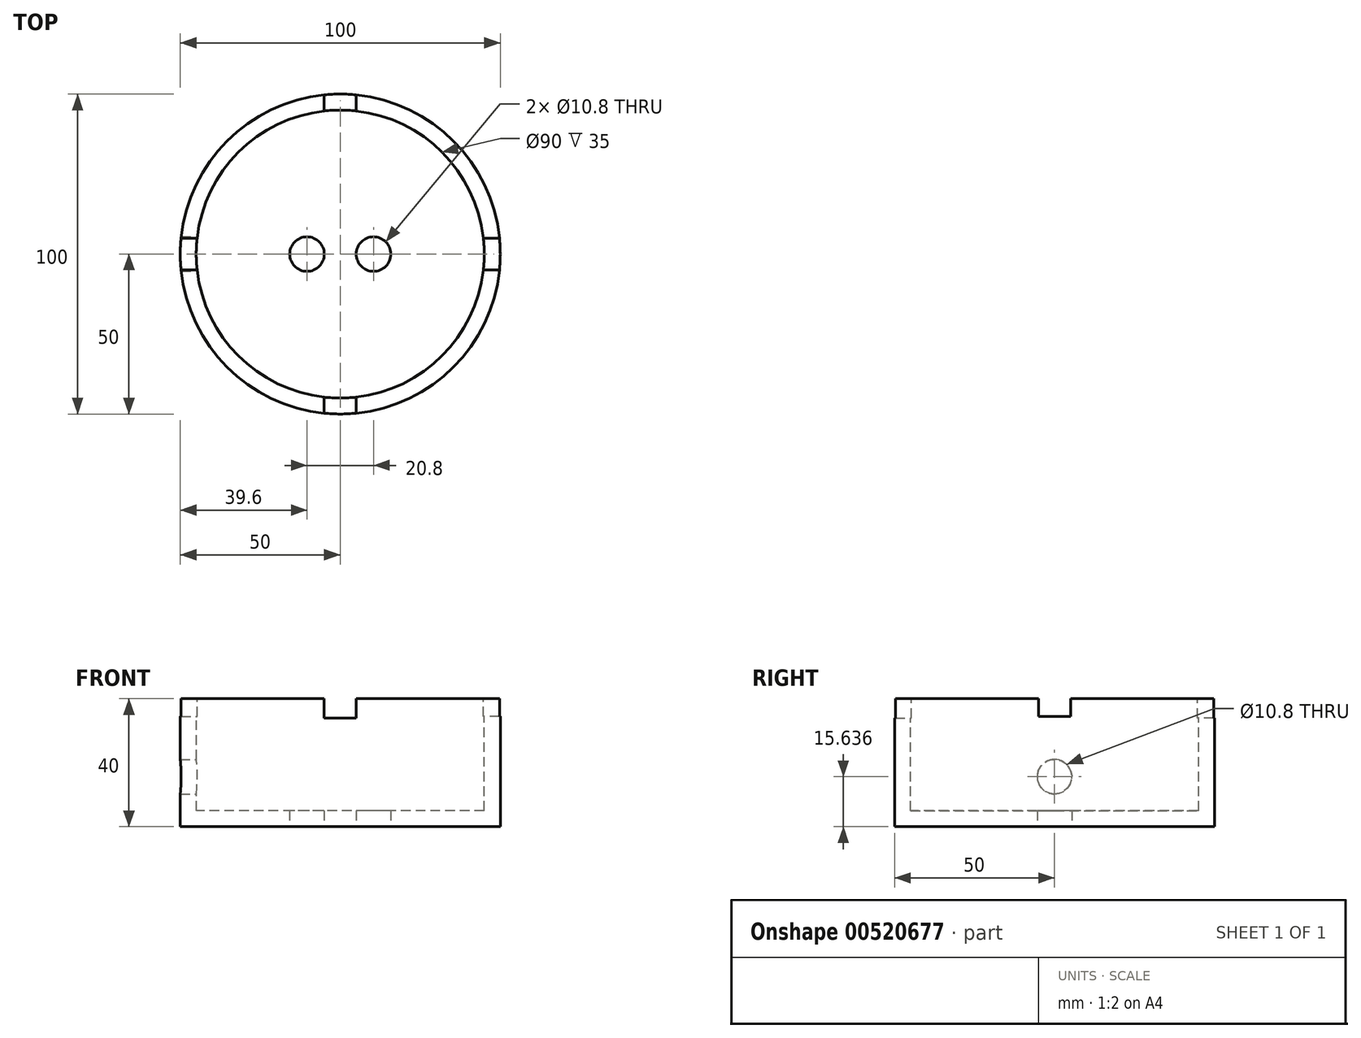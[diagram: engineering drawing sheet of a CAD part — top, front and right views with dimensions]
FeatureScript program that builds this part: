
annotation { "Feature Type Name" : "Feature", "Feature Type Description" : "" }
export const myFeature = defineFeature(function(context is Context, id is Id, definition is map)
    precondition{}
    {
        {
            var Q0;
            Q0=qCreatedBy(makeId("Top.planeOp"),FACE);
            var sketch = newSketch(context, id + "F0", { "sketchPlane" : qUnion([Q0])});
            skCircle(sketch, "E0", {"center": v(0, 0) * mm, "radius": 50 * mm});
            skSolve(sketch);
        }
        {
            var Q0;
            Q0=qSketchRegion(id+"F0",true);
            extrude(context, id + "F1", {"entities" : qUnion([Q0]), "depth" : 40 * mm, "offsetDistance" : 25 * mm});
        }
        {
            var Q0;
            Q0=makeQuery(id+"F1.opExtrude","CAP_FACE",FACE,{"disambiguationData":[OSD([sQuery(id+"F0.wireOp",EDGE,"E0")])],"isStart":false});
            var sketch = newSketch(context, id + "F2", { "sketchPlane" : qUnion([Q0])});
            skCircle(sketch, "E1", {"center": v(0, 0) * mm, "radius": 45 * mm});
            skSolve(sketch);
        }
        {
            var Q0;
            Q0=qSketchRegion(id+"F2",true);
            extrude(context, id + "F3", {"entities" : qUnion([Q0]), "operationType" : NewBodyOperationType.REMOVE, "oppositeDirection" : true, "depth" : 35 * mm, "offsetDistance" : 25 * mm});
        }
        {
            var Q0;
            Q0=qCreatedBy(makeId("Front.planeOp"),FACE);
            var sketch = newSketch(context, id + "F4", { "sketchPlane" : qUnion([Q0])});
            skLineSegment(sketch, "E2.bottom", {"start": v(5, 40) * mm, "end": v(-5, 40) * mm});
            skLineSegment(sketch, "E2.top", {"start": v(5, 34) * mm, "end": v(-5, 34) * mm});
            skLineSegment(sketch, "E2.left", {"start": v(5, 40) * mm, "end": v(5, 34) * mm});
            skLineSegment(sketch, "E2.right", {"start": v(-5, 40) * mm, "end": v(-5, 34) * mm});
            skSolve(sketch);
        }
        {
            var Q0;
            Q0=qSketchRegion(id+"F4",true);
            extrude(context, id + "F5", {"entities" : qUnion([Q0]), "operationType" : NewBodyOperationType.REMOVE, "oppositeDirection" : true, "depth" : 50 * mm, "offsetDistance" : 25 * mm});
        }
        {
            var Q0;
            Q0=qCreatedBy(makeId("Front.planeOp"),FACE);
            var sketch = newSketch(context, id + "F6", { "sketchPlane" : qUnion([Q0])});
            skLineSegment(sketch, "E3.bottom", {"start": v(5, 40) * mm, "end": v(-5, 40) * mm});
            skLineSegment(sketch, "E3.top", {"start": v(5, 34) * mm, "end": v(-5, 34) * mm});
            skLineSegment(sketch, "E3.left", {"start": v(5, 40) * mm, "end": v(5, 34) * mm});
            skLineSegment(sketch, "E3.right", {"start": v(-5, 40) * mm, "end": v(-5, 34) * mm});
            skSolve(sketch);
        }
        {
            var Q0;
            Q0=qSketchRegion(id+"F6",true);
            extrude(context, id + "F7", {"entities" : qUnion([Q0]), "operationType" : NewBodyOperationType.REMOVE, "depth" : 50 * mm, "offsetDistance" : 25 * mm});
        }
        {
            var Q0;
            Q0=qCreatedBy(makeId("Right.planeOp"),FACE);
            var sketch = newSketch(context, id + "F8", { "sketchPlane" : qUnion([Q0])});
            skLineSegment(sketch, "E4.bottom", {"start": v(5, 40) * mm, "end": v(-5, 40) * mm});
            skLineSegment(sketch, "E4.top", {"start": v(5, 34.5) * mm, "end": v(-5, 34.5) * mm});
            skLineSegment(sketch, "E4.left", {"start": v(5, 40) * mm, "end": v(5, 34.5) * mm});
            skLineSegment(sketch, "E4.right", {"start": v(-5, 40) * mm, "end": v(-5, 34.5) * mm});
            skSolve(sketch);
        }
        {
            var Q0;
            Q0=qSketchRegion(id+"F8",true);
            extrude(context, id + "F9", {"entities" : qUnion([Q0]), "operationType" : NewBodyOperationType.REMOVE, "oppositeDirection" : true, "depth" : 50 * mm, "offsetDistance" : 25 * mm});
        }
        {
            var Q0;
            Q0=qCreatedBy(makeId("Right.planeOp"),FACE);
            var sketch = newSketch(context, id + "F10", { "sketchPlane" : qUnion([Q0])});
            skLineSegment(sketch, "E5.bottom", {"start": v(5, 40) * mm, "end": v(-5, 40) * mm});
            skLineSegment(sketch, "E5.top", {"start": v(5, 34.5) * mm, "end": v(-5, 34.5) * mm});
            skLineSegment(sketch, "E5.left", {"start": v(5, 40) * mm, "end": v(5, 34.5) * mm});
            skLineSegment(sketch, "E5.right", {"start": v(-5, 40) * mm, "end": v(-5, 34.5) * mm});
            skSolve(sketch);
        }
        {
            var Q0;
            Q0=qSketchRegion(id+"F10",true);
            extrude(context, id + "F11", {"entities" : qUnion([Q0]), "operationType" : NewBodyOperationType.REMOVE, "depth" : 50 * mm, "offsetDistance" : 25 * mm});
        }
        {
            var Q0;
            Q0=qCreatedBy(makeId("Right.planeOp"),FACE);
            var sketch = newSketch(context, id + "F12", { "sketchPlane" : qUnion([Q0])});
            skCircle(sketch, "E6", {"center": v(0, 15.64) * mm, "radius": 5.4 * mm});
            skSolve(sketch);
        }
        {
            var Q0;
            Q0=qSketchRegion(id+"F12",true);
            extrude(context, id + "F13", {"entities" : qUnion([Q0]), "operationType" : NewBodyOperationType.REMOVE, "oppositeDirection" : true, "depth" : 55 * mm, "offsetDistance" : 25 * mm});
        }
        {
            var Q0;
            Q0=qCreatedBy(makeId("Top.planeOp"),FACE);
            var sketch = newSketch(context, id + "F14", { "sketchPlane" : qUnion([Q0])});
            skCircle(sketch, "E7", {"center": v(-10.4, 0) * mm, "radius": 5.4 * mm});
            skCircle(sketch, "E8", {"center": v(10.4, 0) * mm, "radius": 5.4 * mm});
            skSolve(sketch);
        }
        {
            var Q0;
            Q0 = qSketchRegion(id + "F14", true);
            extrude(context, id + "F15", {"entities" : qUnion([Q0]), "operationType" : NewBodyOperationType.REMOVE, "depth" : 6 * mm, "offsetDistance" : 25 * mm});
        }
    });
